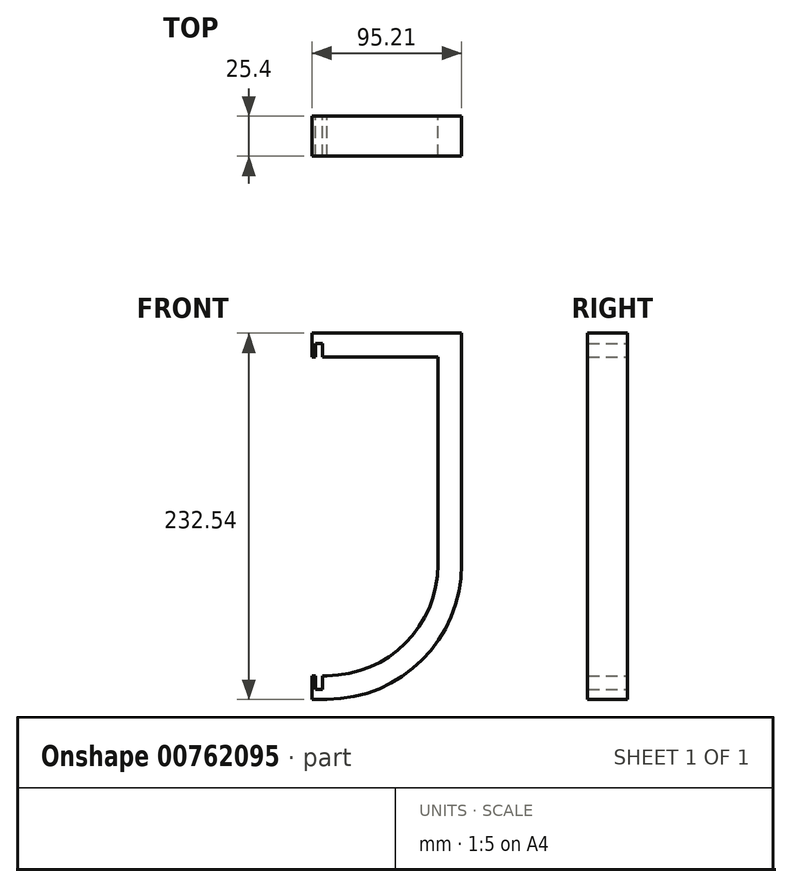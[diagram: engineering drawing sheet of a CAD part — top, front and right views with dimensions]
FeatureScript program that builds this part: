
annotation { "Feature Type Name" : "Feature", "Feature Type Description" : "" }
export const myFeature = defineFeature(function(context is Context, id is Id, definition is map)
    precondition{}
    {
        {
            var Q0;
            Q0=qCreatedBy(makeId("Front.planeOp"),FACE);
            var sketch = newSketch(context, id + "F0", { "sketchPlane" : qUnion([Q0])});
            skArc(sketch, "E0", {"start": v(0, -85.68) * mm, "mid": v(60.58, -60.58) * mm, "end": v(85.68, 0) * mm});
            skArc(sketch, "E1", {"start": v(0, -70.64) * mm, "mid": v(49.95, -49.95) * mm, "end": v(70.64, 0) * mm});
            skPoint(sketch, "E2", {"position": v(85.68, 0) * mm});
            skPoint(sketch, "E3", {"position": v(70.64, 0) * mm});
            skPoint(sketch, "E4", {"position": v(0, -85.68) * mm});
            skPoint(sketch, "E5", {"position": v(0, -70.64) * mm});
            skLineSegment(sketch, "E6", {"start": v(85.68, 0) * mm, "end": v(70.64, 0) * mm});
            skLineSegment(sketch, "E7", {"start": v(0, -70.64) * mm, "end": v(0, -85.68) * mm});
            skLineSegment(sketch, "E8.bottom", {"start": v(0, -70.64) * mm, "end": v(-2.75, -70.64) * mm});
            skLineSegment(sketch, "E8.right", {"start": v(-9.53, -70.64) * mm, "end": v(-9.53, -85.68) * mm});
            skPoint(sketch, "E9", {"position": v(-2.75, -70.64) * mm});
            skPoint(sketch, "E10", {"position": v(-2.75, -79.27) * mm});
            skPoint(sketch, "E11", {"position": v(-7.32, -79.27) * mm});
            skPoint(sketch, "E12", {"position": v(-7.32, -70.64) * mm});
            skLineSegment(sketch, "E13.trimOffspring", {"start": v(-7.32, -70.64) * mm, "end": v(-9.53, -70.64) * mm});
            skLineSegment(sketch, "E14", {"start": v(-2.75, -70.64) * mm, "end": v(-2.75, -79.27) * mm});
            skLineSegment(sketch, "E15", {"start": v(-2.75, -79.27) * mm, "end": v(-7.32, -79.27) * mm});
            skLineSegment(sketch, "E16", {"start": v(-7.32, -79.27) * mm, "end": v(-7.32, -70.64) * mm});
            skLineSegment(sketch, "E17.top", {"start": v(85.68, 146.86) * mm, "end": v(70.64, 146.86) * mm});
            skLineSegment(sketch, "E17.left", {"start": v(85.68, 0) * mm, "end": v(85.68, 146.86) * mm});
            skLineSegment(sketch, "E17.right", {"start": v(70.64, 0) * mm, "end": v(70.64, 131.83) * mm});
            skLineSegment(sketch, "E18.bottom", {"start": v(85.68, 146.86) * mm, "end": v(0, 146.86) * mm});
            skLineSegment(sketch, "E18.top", {"start": v(70.64, 131.83) * mm, "end": v(0, 131.83) * mm});
            skLineSegment(sketch, "E18.left", {"start": v(85.68, 146.86) * mm, "end": v(85.68, 131.83) * mm});
            skLineSegment(sketch, "E18.right", {"start": v(0, 146.86) * mm, "end": v(0, 131.83) * mm});
            skPoint(sketch, "E19", {"position": v(70.64, 146.86) * mm});
            skPoint(sketch, "E20", {"position": v(70.64, 131.83) * mm});
            skPoint(sketch, "E21", {"position": v(85.68, 131.83) * mm});
            skLineSegment(sketch, "E22.bottom", {"start": v(0, 146.86) * mm, "end": v(-9.5, 146.86) * mm});
            skLineSegment(sketch, "E22.right", {"start": v(-9.5, 146.86) * mm, "end": v(-9.5, 131.83) * mm});
            skLineSegment(sketch, "E23", {"start": v(-9.5, 131.83) * mm, "end": v(-7.28, 131.83) * mm});
            skPoint(sketch, "E24", {"position": v(-7.28, 131.83) * mm});
            skPoint(sketch, "E25", {"position": v(-2.7, 131.83) * mm});
            skLineSegment(sketch, "E26.trimOffspring", {"start": v(-7.28, 131.83) * mm, "end": v(-9.5, 131.83) * mm});
            skLineSegment(sketch, "E27", {"start": v(-7.28, 131.83) * mm, "end": v(-7.28, 140.46) * mm});
            skLineSegment(sketch, "E28", {"start": v(-2.7, 131.83) * mm, "end": v(-2.7, 140.46) * mm});
            skLineSegment(sketch, "E29", {"start": v(-2.7, 140.46) * mm, "end": v(-7.28, 140.46) * mm});
            skLineSegment(sketch, "E30", {"start": v(0, -85.68) * mm, "end": v(-9.53, -85.68) * mm});
            skLineSegment(sketch, "E31", {"start": v(0, 131.83) * mm, "end": v(-2.7, 131.83) * mm});
            skSolve(sketch);
        }
        {
            var Q0;
            {var subQ0=sQuery(id+"F0.wireOp",EDGE,"E0");Q0=makeQuery(id+"F0.imprint","IMPRINT",FACE,{"disambiguationData":[TD([[makeQuery(id+"F0.imprint","IMPRINT",EDGE,{"derivedFrom":subQ0}),1.0]])]});}
            var Q1;
            {var subQ1=sQuery(id+"F0.wireOp",EDGE,"E17.left");Q1=makeQuery(id+"F0.imprint","IMPRINT",FACE,{"disambiguationData":[TD([[makeQuery(id+"F0.imprint","IMPRINT",EDGE,{"derivedFrom":subQ1}),1.0]])]});}
            var Q2;
            Q2=makeQuery(id+"F0.imprint","IMPRINT",FACE,{"disambiguationData":[TD([[makeQuery(id+"F0.imprint","IMPRINT",EDGE,{"derivedFrom":sQuery(id+"F0.wireOp",EDGE,"E22.bottom")}),1.0]])]});
            var Q3;
            {var subQ3=sQuery(id+"F0.wireOp",EDGE,"E8.bottom");Q3=makeQuery(id+"F0.imprint","IMPRINT",FACE,{"disambiguationData":[TD([[makeQuery(id+"F0.imprint","IMPRINT",EDGE,{"derivedFrom":subQ3}),1.0]])]});}
            extrude(context, id + "F1", {"entities" : qUnion([Q0, Q1, Q2, Q3]), "depth" : 25.4 * mm, "offsetDistance" : 25.4 * mm});
        }
    });
